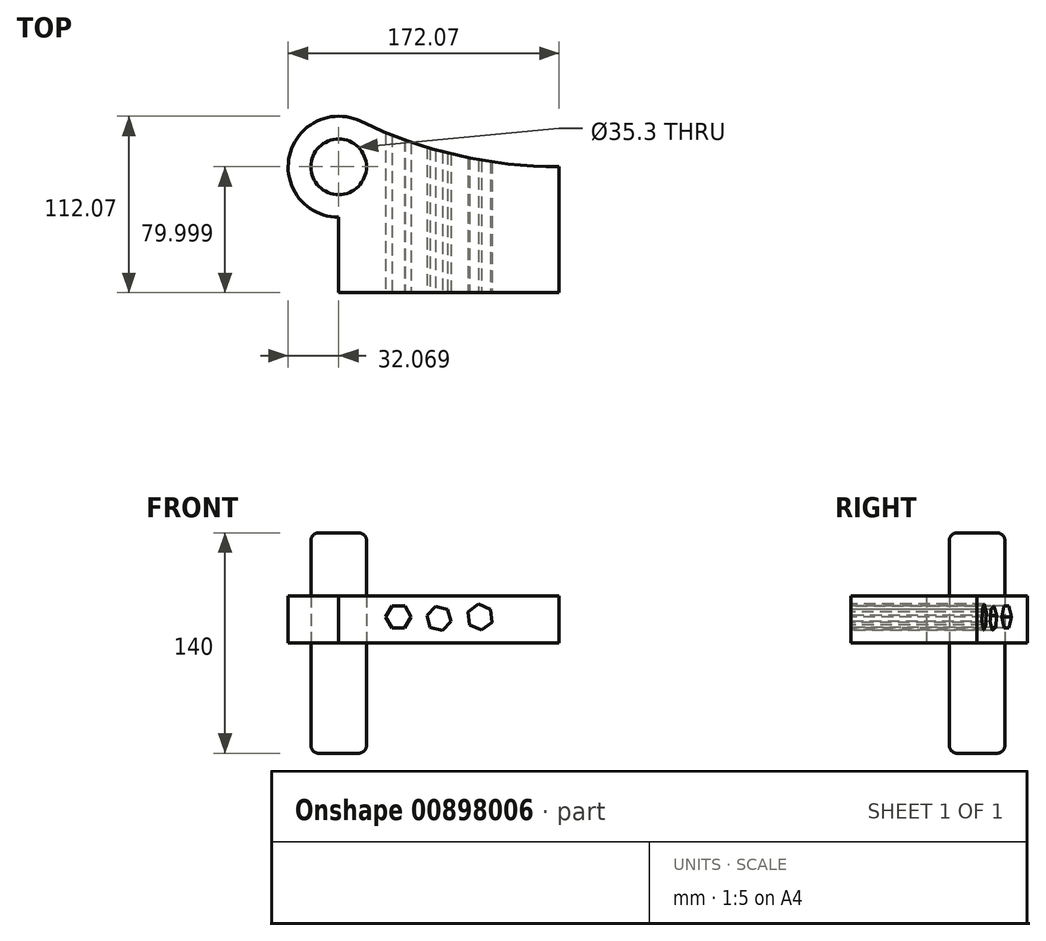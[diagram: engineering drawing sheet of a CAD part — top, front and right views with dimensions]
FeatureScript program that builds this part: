
annotation { "Feature Type Name" : "Feature", "Feature Type Description" : "" }
export const myFeature = defineFeature(function(context is Context, id is Id, definition is map)
    precondition{}
    {
        {
            var Q0;
            Q0=qCreatedBy(makeId("Top.planeOp"),FACE);
            var sketch = newSketch(context, id + "F0", { "sketchPlane" : qUnion([Q0])});
            skLineSegment(sketch, "E0.bottom", {"start": v(-67.98, 37.74) * mm, "end": v(72.02, 37.74) * mm});
            skLineSegment(sketch, "E0.top", {"start": v(-67.98, -42.26) * mm, "end": v(72.02, -42.26) * mm});
            skLineSegment(sketch, "E0.left", {"start": v(-67.98, 37.74) * mm, "end": v(-67.98, -42.26) * mm});
            skLineSegment(sketch, "E0.right", {"start": v(72.02, 37.74) * mm, "end": v(72.02, -42.26) * mm});
            skCircle(sketch, "E1", {"center": v(-67.98, 37.74) * mm, "radius": 32.07 * mm});
            skArc(sketch, "E2", {"start": v(-54.02, 66.61) * mm, "mid": v(7.37, 45.05) * mm, "end": v(72.02, 37.74) * mm});
            skCircle(sketch, "E3", {"center": v(-67.98, 37.74) * mm, "radius": 17.65 * mm});
            skSolve(sketch);
        }
        {
            var Q0;
            {var subQ4=sQuery(id+"F0.wireOp",EDGE,"E0.bottom");var subQ6=sQuery(id+"F0.wireOp",EDGE,"E3");var subQ8=makeQuery(id+"F0.imprint","INTERSECT",VERTEX,{"derivedFrom":[subQ4,subQ6]});Q0=makeQuery(id+"F0.imprint","IMPRINT",FACE,{"disambiguationData":[TD([[makeQuery(id+"F0.imprint","IMPRINT",EDGE,{"disambiguationData":[TD([[subQ8,-1.0]])],"derivedFrom":subQ4}),1.0]])]});}
            var Q1;
            {var subQ0=sQuery(id+"F0.wireOp",EDGE,"E2");Q1=makeQuery(id+"F0.imprint","IMPRINT",FACE,{"disambiguationData":[TD([[makeQuery(id+"F0.imprint","IMPRINT",EDGE,{"derivedFrom":subQ0}),-1.0]])]});}
            var Q2;
            {var subQ1=sQuery(id+"F0.wireOp",EDGE,"E0.top");Q2=makeQuery(id+"F0.imprint","IMPRINT",FACE,{"disambiguationData":[TD([[makeQuery(id+"F0.imprint","IMPRINT",EDGE,{"derivedFrom":subQ1}),1.0]])]});}
            var Q3;
            {var subQ0=sQuery(id+"F0.wireOp",EDGE,"E3");var subQ1=sQuery(id+"F0.wireOp",EDGE,"E0.bottom");var subQ2=makeQuery(id+"F0.imprint","INTERSECT",VERTEX,{"derivedFrom":[subQ1,subQ0]});Q3=makeQuery(id+"F0.imprint","IMPRINT",FACE,{"disambiguationData":[TD([[makeQuery(id+"F0.imprint","IMPRINT",EDGE,{"disambiguationData":[TD([[subQ2,-1.0]])],"derivedFrom":subQ1}),-1.0]])]});}
            extrude(context, id + "F1", {"entities" : qUnion([Q0, Q1, Q2, Q3]), "depth" : 30 * mm, "offsetDistance" : 25 * mm});
        }
        {
            var Q0;
            {var subQ0=sQuery(id+"F0.wireOp",EDGE,"E0.left");var subQ1=sQuery(id+"F0.wireOp",EDGE,"E0.bottom");var subQ2=makeQuery(id+"F0.imprint","INTERSECT",VERTEX,{"derivedFrom":[subQ1,subQ0]});Q0=makeQuery(id+"F0.imprint","IMPRINT",FACE,{"disambiguationData":[TD([[makeQuery(id+"F0.imprint","IMPRINT",EDGE,{"disambiguationData":[TD([[subQ2,-1.0]])],"derivedFrom":subQ1}),-1.0]])]});}
            var Q1;
            {var subQ0=sQuery(id+"F0.wireOp",EDGE,"E0.left");var subQ1=sQuery(id+"F0.wireOp",EDGE,"E0.bottom");var subQ2=makeQuery(id+"F0.imprint","INTERSECT",VERTEX,{"derivedFrom":[subQ1,subQ0]});Q1=makeQuery(id+"F0.imprint","IMPRINT",FACE,{"disambiguationData":[TD([[makeQuery(id+"F0.imprint","IMPRINT",EDGE,{"disambiguationData":[TD([[subQ2,-1.0]])],"derivedFrom":subQ1}),1.0]])]});}
            extrude(context, id + "F2", {"entities" : qUnion([Q0, Q1]), "endBound" : BoundingType.SYMMETRIC, "depth" : 140 * mm, "offsetDistance" : 25 * mm});
        }
        {
            var Q0;
            Q0=makeQuery(id+"F1.opExtrude","SWEPT_FACE",FACE,{"disambiguationData":[OSD([sQuery(id+"F0.wireOp",EDGE,"E0.top")])]});
            var sketch = newSketch(context, id + "F3", { "sketchPlane" : qUnion([Q0])});
            skCircle(sketch, "E4.cCircle", {"center": v(-4.3, 15.68) * mm, "radius": 6.9 * mm, "construction": true});
            skLineSegment(sketch, "E4.0", {"start": v(-6.48, 23.35) * mm, "end": v(-12.03, 17.63) * mm});
            skLineSegment(sketch, "E4.1", {"start": v(1.25, 21.4) * mm, "end": v(-6.48, 23.35) * mm});
            skLineSegment(sketch, "E4.2", {"start": v(3.43, 13.74) * mm, "end": v(1.25, 21.4) * mm});
            skLineSegment(sketch, "E4.3", {"start": v(-2.12, 8.02) * mm, "end": v(3.43, 13.74) * mm});
            skLineSegment(sketch, "E4.4", {"start": v(-9.85, 9.97) * mm, "end": v(-2.12, 8.02) * mm});
            skLineSegment(sketch, "E4.5", {"start": v(-12.03, 17.63) * mm, "end": v(-9.85, 9.97) * mm});
            skPoint(sketch, "E4.0.midPoint", {"position": v(-9.25, 20.5) * mm});
            skCircle(sketch, "E5.cCircle", {"center": v(21.87, 16.47) * mm, "radius": 7.2 * mm, "construction": true});
            skLineSegment(sketch, "E5.0", {"start": v(29.54, 13.23) * mm, "end": v(22.9, 8.21) * mm});
            skLineSegment(sketch, "E5.1", {"start": v(22.9, 8.21) * mm, "end": v(15.23, 11.46) * mm});
            skLineSegment(sketch, "E5.2", {"start": v(15.23, 11.46) * mm, "end": v(14.21, 19.72) * mm});
            skLineSegment(sketch, "E5.3", {"start": v(14.21, 19.72) * mm, "end": v(20.86, 24.74) * mm});
            skLineSegment(sketch, "E5.4", {"start": v(20.86, 24.74) * mm, "end": v(28.52, 21.49) * mm});
            skLineSegment(sketch, "E5.5", {"start": v(28.52, 21.49) * mm, "end": v(29.54, 13.23) * mm});
            skPoint(sketch, "E5.0.midPoint", {"position": v(26.22, 10.72) * mm});
            skCircle(sketch, "E6.cCircle", {"center": v(-30.09, 16.56) * mm, "radius": 7.04 * mm, "construction": true});
            skLineSegment(sketch, "E6.0", {"start": v(-21.96, 16.52) * mm, "end": v(-26.06, 9.5) * mm});
            skLineSegment(sketch, "E6.1", {"start": v(-26.06, 9.5) * mm, "end": v(-34.18, 9.54) * mm});
            skLineSegment(sketch, "E6.2", {"start": v(-34.18, 9.54) * mm, "end": v(-38.2, 16.6) * mm});
            skLineSegment(sketch, "E6.3", {"start": v(-38.2, 16.6) * mm, "end": v(-34.11, 23.61) * mm});
            skLineSegment(sketch, "E6.4", {"start": v(-34.11, 23.61) * mm, "end": v(-26, 23.57) * mm});
            skLineSegment(sketch, "E6.5", {"start": v(-26, 23.57) * mm, "end": v(-21.96, 16.52) * mm});
            skPoint(sketch, "E6.0.midPoint", {"position": v(-24, 13.01) * mm});
            skSolve(sketch);
        }
        {
            var Q0;
            Q0=makeQuery(id+"F3.imprint","IMPRINT",FACE,{"disambiguationData":[TD([[makeQuery(id+"F3.imprint","IMPRINT",EDGE,{"derivedFrom":sQuery(id+"F3.wireOp",EDGE,"E6.0")}),-1.0]])]});
            var Q1;
            Q1=makeQuery(id+"F3.imprint","IMPRINT",FACE,{"disambiguationData":[TD([[makeQuery(id+"F3.imprint","IMPRINT",EDGE,{"derivedFrom":sQuery(id+"F3.wireOp",EDGE,"E4.0")}),1.0]])]});
            var Q2;
            Q2=makeQuery(id+"F3.imprint","IMPRINT",FACE,{"disambiguationData":[TD([[makeQuery(id+"F3.imprint","IMPRINT",EDGE,{"derivedFrom":sQuery(id+"F3.wireOp",EDGE,"E5.0")}),-1.0]])]});
            extrude(context, id + "F4", {"entities" : qUnion([Q0, Q1, Q2]), "operationType" : NewBodyOperationType.REMOVE, "oppositeDirection" : true, "depth" : 200 * mm, "offsetDistance" : 25 * mm});
        }
        {
            var Q0;
            Q0=makeQuery(id+"F2.opExtrude","SWEPT_FACE",FACE,{"disambiguationData":[OSD([sQuery(id+"F0.wireOp",EDGE,"E3")])]});
            fillet(context, id + "F5", {"entities" : qUnion([Q0]), "radius" : 5 * mm, "tangentPropagation" : true, "allowEdgeOverflow" : false});
        }
    });
